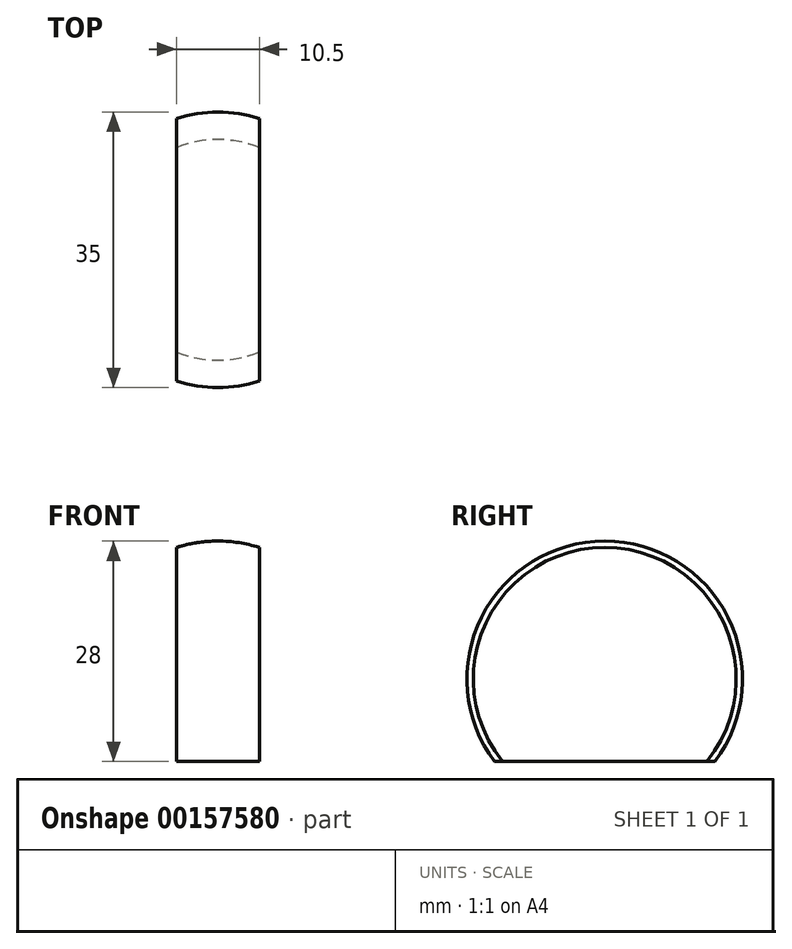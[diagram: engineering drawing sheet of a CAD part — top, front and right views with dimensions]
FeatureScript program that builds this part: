
annotation { "Feature Type Name" : "Feature", "Feature Type Description" : "" }
export const myFeature = defineFeature(function(context is Context, id is Id, definition is map)
    precondition{}
    {
        {
            var Q0;
            Q0=qCreatedBy(makeId("Front.planeOp"),FACE);
            var sketch = newSketch(context, id + "F0", { "sketchPlane" : qUnion([Q0])});
            skCircle(sketch, "E0", {"center": v(0, -17.5) * mm, "radius": 17.5 * mm});
            skLineSegment(sketch, "E1", {"start": v(0, -35) * mm, "end": v(0, 0) * mm});
            skSolve(sketch);
        }
        {
            var Q0;
            {var subQ0=sQuery(id+"F0.wireOp",EDGE,"E1");Q0=makeQuery(id+"F0.imprint","IMPRINT",FACE,{"disambiguationData":[TD([[makeQuery(id+"F0.imprint","IMPRINT",EDGE,{"derivedFrom":subQ0}),-1.0]])]});}
            var Q1;
            Q1=sQuery(id+"F0.wireOp",EDGE,"E1");
            revolve(context, id + "F1", {"entities" : qUnion([Q0]), "axis" : qUnion([Q1]), "revolveType" : RevolveType.FULL});
        }
        {
            var Q0;
            Q0=qCreatedBy(makeId("Top.planeOp"),FACE);
            var sketch = newSketch(context, id + "F2", { "sketchPlane" : qUnion([Q0])});
            skLineSegment(sketch, "E2.bottom", {"start": v(5.25, 17.5) * mm, "end": v(-5.25, 17.5) * mm});
            skLineSegment(sketch, "E2.top", {"start": v(5.25, -17.5) * mm, "end": v(-5.25, -17.5) * mm});
            skLineSegment(sketch, "E2.left", {"start": v(5.25, 17.5) * mm, "end": v(5.25, -17.5) * mm});
            skLineSegment(sketch, "E2.right", {"start": v(-5.25, 17.5) * mm, "end": v(-5.25, -17.5) * mm});
            skPoint(sketch, "E2.middle", {"position": v(0, 0) * mm});
            skSolve(sketch);
        }
        {
            var Q0;
            Q0=qSketchRegion(id+"F2",true);
            extrude(context, id + "F3", {"entities" : qUnion([Q0]), "oppositeDirection" : true, "depth" : 28 * mm});
        }
        {
            var Q0;
            Q0=makeQuery(id+"F1.opRevolve","SWEPT_BODY",BODY,{"disambiguationData":[OSD([sQuery(id+"F0.wireOp",EDGE,"E0"),sQuery(id+"F0.wireOp",EDGE,"E1")])]});
            var Q1;
            Q1=makeQuery(id+"F3.opExtrude","SWEPT_BODY",BODY,{"disambiguationData":[OSD([sQuery(id+"F2.wireOp",EDGE,"E2.bottom"),sQuery(id+"F2.wireOp",EDGE,"E2.top"),sQuery(id+"F2.wireOp",EDGE,"E2.left"),sQuery(id+"F2.wireOp",EDGE,"E2.right")])]});
            booleanBodies(context, id + "F4", {"operationType" : BooleanOperationType.INTERSECTION, "tools" : qUnion([Q0, Q1])});
        }
    });
